# Revit family: RUFO-490-3750-840-Zx
name_source: partatom
category: Leuchten
revit_build: Autodesk Revit 2017 (Build: 20190508_0315(x64)
units: mm (PartAtom-declared; Revit-internal decimal feet)

## family parameters
Basisbauteil = Fläche
Beim Laden mit Abzugskörper schneiden = Ja
Bemaßung runder Anschluss = Durchmesser verwenden
Gemeinsam genutzt = Nein
Lichtquelle = Ja
OmniClass-Nummer = 23.80.70.11
OmniClass-Titel = Luminaries for Internal Lighting
Raumberechnungspunkt = Nein
Teiletyp = Normal

## types (10) — shared parameters
Baugruppenkennzeichen = D5020200
Datei für fotometrisches Netz = RUFO 4903750-840-Z.IES
Emissionsform beim Rendern sichtbar = Nein
Farbfilter = 16777215
Farbtemperaturverschiebung bei Dämpfen der Lampe = <Keine Auswahl>
Hersteller = RIDI Leuchten GmbH
Lampe = LED
Neigungswinkel = 90.00°
Scheinlast = 28 VA
URL = www.ridi.de
Von Kreisdurchmesser aussenden = 460 mm  [stored 1.50919 ft]
brand = RIDI
conformity mark = CE
electrical safety class = 1
height = 95 mm
ingress protection (IP) code = IP20
length = 460 mm  [stored 1.50919 ft]
nominal frequency = 50-60Hz
nominal voltage = 230
rated input power = 28
voltage type (AC, DC, UC) = AC
width = 460 mm  [stored 1.50919 ft]
zero-valued in all types: Vorgabe-Ansicht

## per-type parameters (varying)
| type | Modell | product name | weight |
| RUFO 490/3750-840 Z | 0420772 | RUFO 490/3750-840 Z | 2.1kg |
| RUFO 490/3750-840 Z-DALI | 0430772 | RUFO 490/3750-840 Z-DALI | 2.1kg |
| RUFO 490/3750-840 Z-2K | 0420773 | RUFO 490/3750-840 Z-2K | 2.1kg |
| RUFO 490/3750-840 Z-2K-DALI | 0430773 | RUFO 490/3750-840 Z-2K-DALI | 2.1kg |
| RUFO 490/3750-840 Z-2K-EDS3 | 0420772//377 | RUFO 490/3750-840 Z-2K-RS | 2.5kg |
| RUFO 490/3750-840 Z-2K-RS-EDS3 | 0420773//377396 | RUFO 490/3750-840 Z-2K-RS-EDS3 | 2.1kg |
| RUFO 490/3750-840 Z-EDS3 | 0420772//377 | RUFO 490/3750-840 Z-EDS3 | 2.1kg |
| RUFO 490/3750-840 Z-RS | 0420772//396 | RUFO 490/3750-840 Z-RS | 2.1kg |
| RUFO 490/3750-840 Z-RS-EDS3 | 0420772//377396 | RUFO 490/3750-840 Z-RS-EDS3 | 2.1kg |
| RUFO 490/3750-840 Z-2K-RS | 0420773//396 | RUFO 490/3750-840 Z-2K-RS | 2.1kg |

note: [stored X ft] marks values corroborated as IEEE doubles in the binary element streams (Revit-internal decimal feet)
